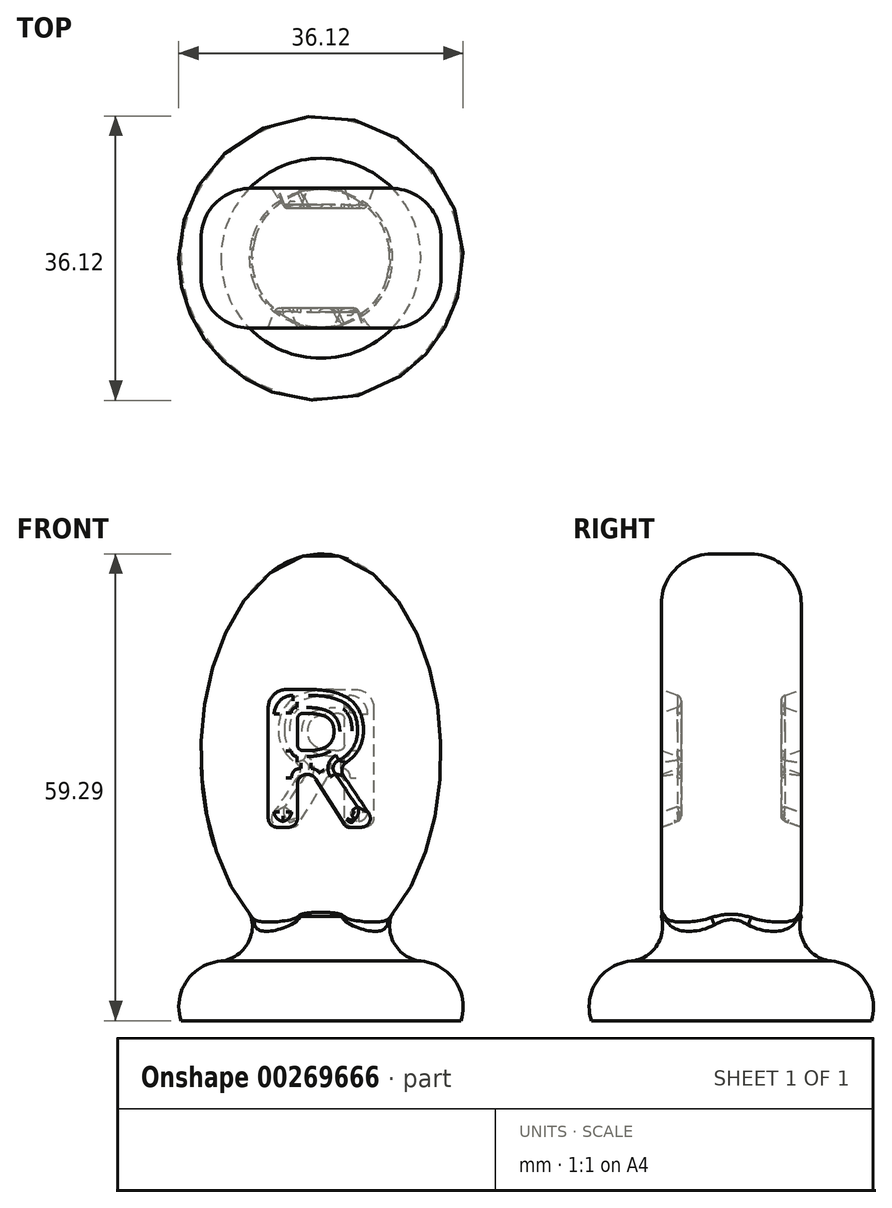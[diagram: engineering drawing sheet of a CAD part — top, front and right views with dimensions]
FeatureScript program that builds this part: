
annotation { "Feature Type Name" : "Feature", "Feature Type Description" : "" }
export const myFeature = defineFeature(function(context is Context, id is Id, definition is map)
    precondition{}
    {
        {
            var Q0;
            Q0=qCreatedBy(makeId("Front.planeOp"),FACE);
            var sketch = newSketch(context, id + "F0", { "sketchPlane" : qUnion([Q0])});
            skEllipse(sketch, "E0", {"center": v(0, 33.89) * mm, "majorRadius": 25.4 * mm, "minorRadius": 15.24 * mm, "majorAxis": v(0, -1)});
            skLineSegment(sketch, "E1", {"start": v(0, 0) * mm, "end": v(0, 8.49) * mm, "construction": true});
            skSolve(sketch);
        }
        {
            var Q0;
            Q0 = qSketchRegion(id + "F0", true);
            extrude(context, id + "F1", {"entities" : qUnion([Q0]), "depth" : 8.9 * mm});
        }
        {
            var Q0;
            Q0=makeQuery(id+"F1.opExtrude","CAP_EDGE",EDGE,{"disambiguationData":[OSD([sQuery(id+"F0.wireOp",EDGE,"E0")])],"isStart":false});
            fillet(context, id + "F2", {"entities" : qUnion([Q0]), "radius" : 6.35 * mm, "tangentPropagation" : true, "allowEdgeOverflow" : false});
        }
        {
            var Q0;
            Q0=qCreatedBy(makeId("Front.planeOp"),FACE);
            var sketch = newSketch(context, id + "F3", { "sketchPlane" : qUnion([Q0])});
            skLineSegment(sketch, "E2", {"start": v(0, 0) * mm, "end": v(-17.78, 0) * mm});
            skLineSegment(sketch, "E3", {"start": v(-17.78, 0) * mm, "end": v(0, 26.51) * mm});
            skLineSegment(sketch, "E4", {"start": v(0, 26.51) * mm, "end": v(0, 0) * mm});
            skArc(sketch, "E5", {"start": v(-12.7, 7.57) * mm, "mid": v(-17.07, 5.02) * mm, "end": v(-17.78, 0) * mm});
            skArc(sketch, "E6", {"start": v(-12.7, 7.57) * mm, "mid": v(-9.48, 9.53) * mm, "end": v(-8.9, 13.26) * mm});
            skLineSegment(sketch, "E7", {"start": v(0, 0) * mm, "end": v(0, -19.3) * mm, "construction": true});
            skSolve(sketch);
        }
        {
            var Q0;
            {var subQ0=sQuery(id+"F3.wireOp",EDGE,"E5");Q0=makeQuery(id+"F3.imprint","IMPRINT",FACE,{"disambiguationData":[TD([[makeQuery(id+"F3.imprint","IMPRINT",EDGE,{"derivedFrom":subQ0}),1.0]])]});}
            var Q1;
            {var subQ4=sQuery(id+"F3.wireOp",EDGE,"E2");Q1=makeQuery(id+"F3.imprint","IMPRINT",FACE,{"disambiguationData":[TD([[makeQuery(id+"F3.imprint","IMPRINT",EDGE,{"derivedFrom":subQ4}),-1.0]])]});}
            var Q2;
            Q2=sQuery(id+"F3.wireOp",EDGE,"E7");
            revolve(context, id + "F4", {"entities" : qUnion([Q0, Q1]), "axis" : qUnion([Q2]), "revolveType" : RevolveType.ONE_DIRECTION, "oppositeDirection" : true, "angle" : 180 * degree});
        }
        {
            var Q0;
            Q0=makeQuery(id+"F1.opExtrude","CAP_FACE",FACE,{"disambiguationData":[OSD([sQuery(id+"F0.wireOp",EDGE,"E0")])],"isStart":false});
            var sketch = newSketch(context, id + "F5", { "sketchPlane" : qUnion([Q0])});
            skSolve(sketch);
        }
        {
            var Q0;
            {var subQ0=sQuery(id+"F0.wireOp",EDGE,"E0");Q0=makeQuery(id+"F5.imprint","IMPRINT",FACE,{"disambiguationData":[TD([[makeQuery(id+"F5.imprint","IMPRINT",EDGE,{"derivedFrom":makeQuery(id+"F2.opFillet","BLEND_EDGE",EDGE,{"blendedFrom":[makeQuery(id+"F1.opExtrude","CAP_EDGE",EDGE,{"disambiguationData":[OSD([subQ0])],"isStart":false}),makeQuery(id+"F1.opExtrude","CAP_FACE",FACE,{"disambiguationData":[OSD([subQ0])],"isStart":false})],"blendedInto":[makeQuery(id+"F1.opExtrude","CAP_FACE",FACE,{"disambiguationData":[OSD([subQ0])],"isStart":false})]})}),1.0]])]});}
            var sketch = newSketch(context, id + "F6", { "sketchPlane" : qUnion([Q0])});
            skText(sketch, "E8", { "text": "R", "fontName": "OpenSans-Bold.ttf"});
            const initialGuessF6  = {"E8": [-0.0089, 0.02457, 1, 0, 0.01766]};
            skSetInitialGuess(sketch, initialGuessF6);
            skSolve(sketch);
        }
        {
            var Q0;
            Q0 = qSketchRegion(id + "F6", true);
            extrude(context, id + "F7", {"entities" : qUnion([Q0]), "operationType" : NewBodyOperationType.REMOVE, "oppositeDirection" : true, "depth" : 2.54 * mm, "hasDraft" : true, "draftAngle" : 20 * degree, "draftPullDirection" : true});
        }
        {
            var Q0;
            Q0=makeQuery(id+"F7.boolean.opBoolean","COPY",EDGE,{"derivedFrom":makeQuery(id+"F7.opExtrude","SWEPT_EDGE",EDGE,{"disambiguationData":[OSD([sQuery(id+"F6.wireOp",EDGE,"E8.sketch_text.stroke-9"),sQuery(id+"F6.wireOp",EDGE,"E8.sketch_text.stroke-10")])]})});
            fillet(context, id + "F8", {"entities" : qUnion([Q0]), "radius" : 2.54 * mm, "tangentPropagation" : true, "allowEdgeOverflow" : false});
        }
        {
            var Q0;
            Q0=makeQuery(id+"F7.boolean.opBoolean","COPY",EDGE,{"derivedFrom":makeQuery(id+"F7.opExtrude","SWEPT_EDGE",EDGE,{"disambiguationData":[OSD([sQuery(id+"F6.wireOp",EDGE,"E8.sketch_text.stroke-15"),sQuery(id+"F6.wireOp",EDGE,"E8.sketch_text.stroke-16")])]})});
            var Q1;
            Q1=makeQuery(id+"F7.boolean.opBoolean","COPY",EDGE,{"derivedFrom":makeQuery(id+"F7.opExtrude","SWEPT_EDGE",EDGE,{"disambiguationData":[OSD([sQuery(id+"F6.wireOp",EDGE,"E8.sketch_text.stroke-14"),sQuery(id+"F6.wireOp",EDGE,"E8.sketch_text.stroke-15")])]})});
            var Q2;
            Q2=makeQuery(id+"F7.boolean.opBoolean","COPY",EDGE,{"derivedFrom":makeQuery(id+"F7.opExtrude","SWEPT_EDGE",EDGE,{"disambiguationData":[OSD([sQuery(id+"F6.wireOp",EDGE,"E8.sketch_text.stroke-8"),sQuery(id+"F6.wireOp",EDGE,"E8.sketch_text.stroke-9")])]})});
            var Q3;
            Q3=makeQuery(id+"F7.boolean.opBoolean","COPY",EDGE,{"derivedFrom":makeQuery(id+"F7.opExtrude","SWEPT_EDGE",EDGE,{"disambiguationData":[OSD([sQuery(id+"F6.wireOp",EDGE,"E8.sketch_text.stroke-7"),sQuery(id+"F6.wireOp",EDGE,"E8.sketch_text.stroke-8")])]})});
            var Q4;
            Q4=makeQuery(id+"F7.boolean.opBoolean","COPY",EDGE,{"derivedFrom":makeQuery(id+"F7.opExtrude","SWEPT_EDGE",EDGE,{"disambiguationData":[OSD([sQuery(id+"F6.wireOp",EDGE,"E8.sketch_text.stroke-7"),sQuery(id+"F6.wireOp",EDGE,"E8.sketch_text.stroke-18")])]})});
            var Q5;
            Q5=makeQuery(id+"F7.boolean.opBoolean","COPY",EDGE,{"derivedFrom":makeQuery(id+"F7.opExtrude","SWEPT_EDGE",EDGE,{"disambiguationData":[OSD([sQuery(id+"F6.wireOp",EDGE,"E8.sketch_text.stroke-17"),sQuery(id+"F6.wireOp",EDGE,"E8.sketch_text.stroke-18")])]})});
            fillet(context, id + "F9", {"entities" : qUnion([Q0, Q1, Q2, Q3, Q4, Q5]), "radius" : 1.27 * mm, "tangentPropagation" : true, "allowEdgeOverflow" : false});
        }
        {
            var Q0;
            Q0=makeQuery(id+"F7.boolean.opBoolean","COPY",EDGE,{"derivedFrom":makeQuery(id+"F7.opExtrude","SWEPT_EDGE",EDGE,{"disambiguationData":[OSD([sQuery(id+"F6.wireOp",EDGE,"E8.sketch_text.stroke-16"),sQuery(id+"F6.wireOp",EDGE,"E8.sketch_text.stroke-17")])]})});
            var Q1;
            Q1=makeQuery(id+"F7.boolean.opBoolean","COPY",EDGE,{"derivedFrom":makeQuery(id+"F7.opExtrude","SWEPT_EDGE",EDGE,{"disambiguationData":[OSD([sQuery(id+"F6.wireOp",EDGE,"E8.sketch_text.stroke-5"),sQuery(id+"F6.wireOp",EDGE,"E8.sketch_text.stroke-6")])]})});
            var Q2;
            Q2=makeQuery(id+"F7.boolean.opBoolean","COPY",EDGE,{"derivedFrom":makeQuery(id+"F7.opExtrude","SWEPT_EDGE",EDGE,{"disambiguationData":[OSD([sQuery(id+"F6.wireOp",EDGE,"E8.sketch_text.stroke-0"),sQuery(id+"F6.wireOp",EDGE,"E8.sketch_text.stroke-6")])]})});
            fillet(context, id + "F10", {"entities" : qUnion([Q0, Q1, Q2]), "radius" : 0.76 * mm, "tangentPropagation" : true, "allowEdgeOverflow" : false});
        }
        {
            var Q0;
            Q0=makeQuery(id+"F7.boolean.opBoolean","COPY",EDGE,{"derivedFrom":makeQuery(id+"F7.opExtrude","CAP_EDGE",EDGE,{"disambiguationData":[OSD([sQuery(id+"F6.wireOp",EDGE,"E8.sketch_text.stroke-6")])],"isStart":false})});
            var Q1;
            Q1=makeQuery(id+"F7.boolean.opBoolean","COPY",EDGE,{"derivedFrom":makeQuery(id+"F7.opExtrude","CAP_EDGE",EDGE,{"disambiguationData":[OSD([sQuery(id+"F6.wireOp",EDGE,"E8.sketch_text.stroke-7")])],"isStart":false})});
            fillet(context, id + "F11", {"entities" : qUnion([Q0, Q1]), "radius" : 0.76 * mm, "tangentPropagation" : true, "allowEdgeOverflow" : false});
        }
        {
            var Q0;
            Q0=makeQuery(id+"F4.opRevolve","SWEPT_BODY",BODY,{"disambiguationData":[OSD([sQuery(id+"F3.wireOp",EDGE,"E2"),sQuery(id+"F3.wireOp",EDGE,"E3"),sQuery(id+"F3.wireOp",EDGE,"E4"),sQuery(id+"F3.wireOp",EDGE,"E5"),sQuery(id+"F3.wireOp",EDGE,"E6")])]});
            var Q1;
            Q1=makeQuery(id+"F1.opExtrude","SWEPT_BODY",BODY,{"disambiguationData":[OSD([sQuery(id+"F0.wireOp",EDGE,"E0")])]});
            booleanBodies(context, id + "F12", {"operationType" : BooleanOperationType.UNION, "tools" : qUnion([Q0, Q1])});
        }
        {
            var Q0;
            Q0=makeQuery(id+"F4.opRevolve","SWEPT_BODY",BODY,{"disambiguationData":[OSD([sQuery(id+"F3.wireOp",EDGE,"E2"),sQuery(id+"F3.wireOp",EDGE,"E3"),sQuery(id+"F3.wireOp",EDGE,"E4"),sQuery(id+"F3.wireOp",EDGE,"E5"),sQuery(id+"F3.wireOp",EDGE,"E6")])]});
            var Q1;
            Q1=sQuery(id+"F3.wireOp",EDGE,"E7");
            circularPattern(context, id + "F13", {"operationType" : NewBodyOperationType.ADD, "entities" : qUnion([Q0]), "axis" : qUnion([Q1]), "angle" : 360 * degree, "instanceCount" : 2, "equalSpace" : true});
        }
        {
            var Q0;
            Q0=makeQuery(id+"F12.opBoolean","INTERSECT",EDGE,{"disambiguationData":[OD(1.0)],"derivedFrom":[makeQuery(id+"F2.opFillet","BLEND_FACE",FACE,{"disambiguationData":[OSD([sQuery(id+"F0.wireOp",EDGE,"E0")])]}),makeQuery(id+"F4.opRevolve","SWEPT_FACE",FACE,{"disambiguationData":[OSD([sQuery(id+"F3.wireOp",EDGE,"E6")])]})]});
            var Q1;
            {var subQ0=makeQuery(id+"F4.opRevolve","SWEPT_FACE",FACE,{"disambiguationData":[OSD([sQuery(id+"F3.wireOp",EDGE,"E6")])]});var subQ1=makeQuery(id+"F1.opExtrude","SWEPT_FACE",FACE,{"disambiguationData":[OSD([sQuery(id+"F0.wireOp",EDGE,"E0")])]});Q1=makeQuery(id+"F13.boolean.opBoolean","MERGE",EDGE,{"derivedFrom":[makeQuery(id+"F12.opBoolean","INTERSECT",EDGE,{"disambiguationData":[OD(1.0)],"derivedFrom":[subQ1,subQ0]}),makeQuery(id+"F13.opPattern","COPY",EDGE,{"derivedFrom":makeQuery(id+"F12.opBoolean","INTERSECT",EDGE,{"disambiguationData":[OD(0.0)],"derivedFrom":[subQ1,subQ0]}),"instanceName":"1"})]});}
            var Q2;
            Q2=makeQuery(id+"F12.opBoolean","INTERSECT",EDGE,{"disambiguationData":[OD(0.0)],"derivedFrom":[makeQuery(id+"F2.opFillet","BLEND_FACE",FACE,{"disambiguationData":[OSD([sQuery(id+"F0.wireOp",EDGE,"E0")])]}),makeQuery(id+"F4.opRevolve","SWEPT_FACE",FACE,{"disambiguationData":[OSD([sQuery(id+"F3.wireOp",EDGE,"E6")])]})]});
            fillet(context, id + "F14", {"entities" : qUnion([Q0, Q1, Q2]), "radius" : 1.52 * mm, "tangentPropagation" : true, "allowEdgeOverflow" : false});
        }
        {
            var Q0;
            Q0=makeQuery(id+"F12.opBoolean","INTERSECT",EDGE,{"derivedFrom":[makeQuery(id+"F2.opFillet","BLEND_FACE",FACE,{"disambiguationData":[OSD([sQuery(id+"F0.wireOp",EDGE,"E0")])]}),makeQuery(id+"F4.opRevolve","SWEPT_FACE",FACE,{"disambiguationData":[OSD([sQuery(id+"F3.wireOp",EDGE,"E3")])]})]});
            var Q1;
            Q1=makeQuery(id+"F13.opPattern","COPY",EDGE,{"derivedFrom":makeQuery(id+"F12.opBoolean","INTERSECT",EDGE,{"derivedFrom":[makeQuery(id+"F2.opFillet","BLEND_FACE",FACE,{"disambiguationData":[OSD([sQuery(id+"F0.wireOp",EDGE,"E0")])]}),makeQuery(id+"F4.opRevolve","SWEPT_FACE",FACE,{"disambiguationData":[OSD([sQuery(id+"F3.wireOp",EDGE,"E3")])]})]}),"instanceName":"1"});
            fillet(context, id + "F15", {"entities" : qUnion([Q0, Q1]), "radius" : 0.76 * mm, "tangentPropagation" : true, "allowEdgeOverflow" : false});
        }
    });
